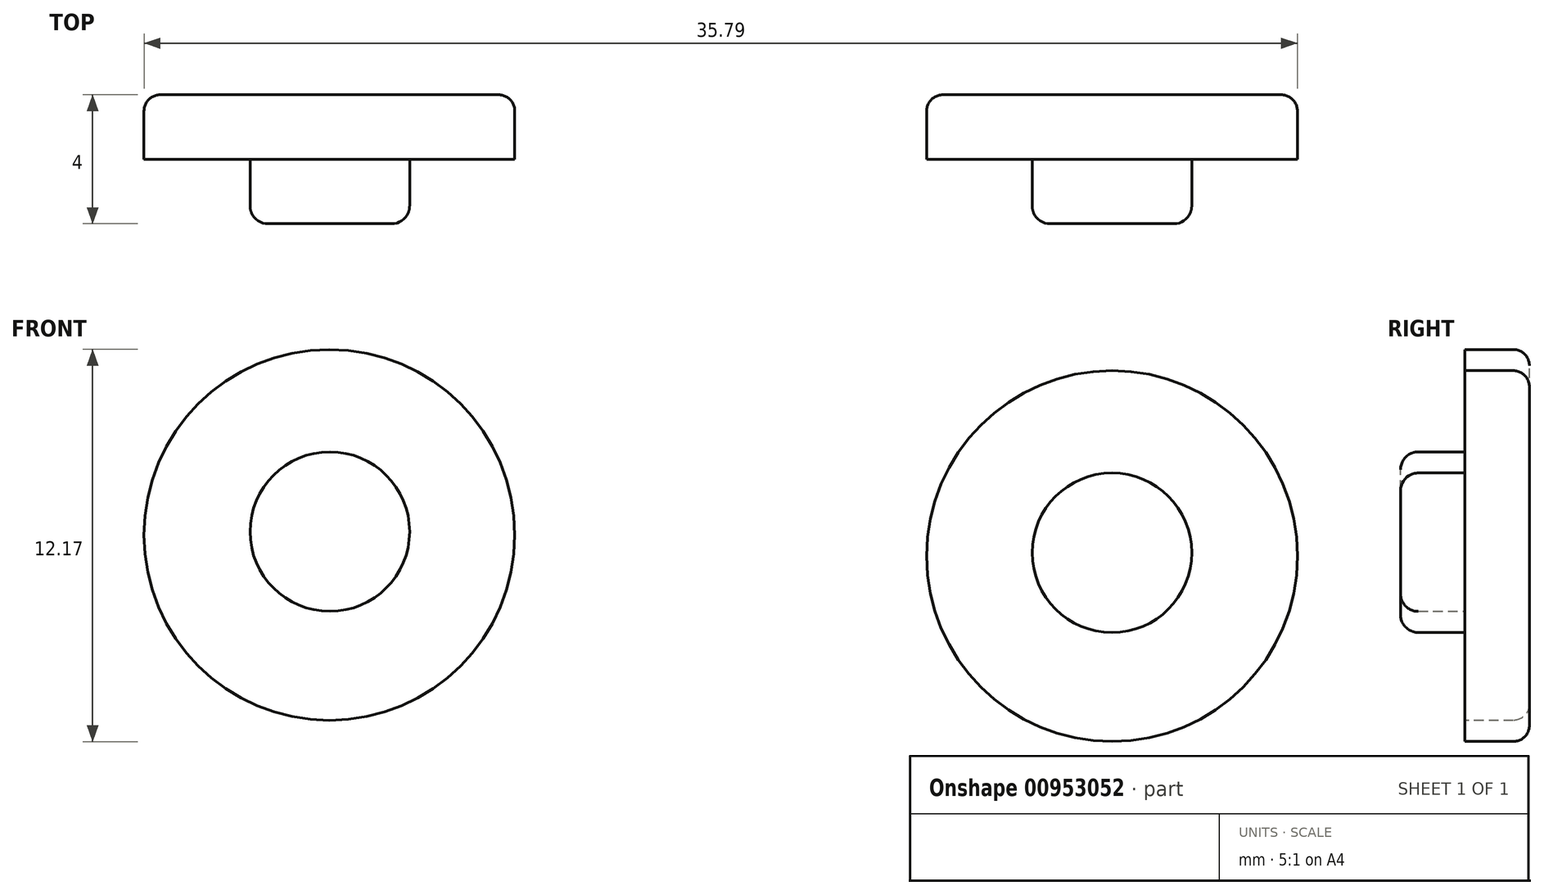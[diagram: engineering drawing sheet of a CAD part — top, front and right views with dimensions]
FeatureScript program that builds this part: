
annotation { "Feature Type Name" : "Feature", "Feature Type Description" : "" }
export const myFeature = defineFeature(function(context is Context, id is Id, definition is map)
    precondition{}
    {
        {
            var Q0;
            Q0=qCreatedBy(makeId("Front.planeOp"),FACE);
            var sketch = newSketch(context, id + "F0", { "sketchPlane" : qUnion([Q0])});
            skCircle(sketch, "E0", {"center": v(-55.31, 54.57) * mm, "radius": 5.75 * mm});
            skCircle(sketch, "E1", {"center": v(-31.02, 53.92) * mm, "radius": 5.75 * mm});
            skSolve(sketch);
        }
        {
            var Q0;
            Q0=makeQuery(id+"F0.imprint","IMPRINT",FACE,{"disambiguationData":[TD([[makeQuery(id+"F0.imprint","IMPRINT",EDGE,{"derivedFrom":sQuery(id+"F0.wireOp",EDGE,"E1")}),1.0]])]});
            var Q1;
            Q1=makeQuery(id+"F0.imprint","IMPRINT",FACE,{"disambiguationData":[TD([[makeQuery(id+"F0.imprint","IMPRINT",EDGE,{"derivedFrom":sQuery(id+"F0.wireOp",EDGE,"E0")}),1.0]])]});
            extrude(context, id + "F1", {"entities" : qUnion([Q0, Q1]), "depth" : -2 * mm, "offsetDistance" : 25.4 * mm});
        }
        {
            var Q0;
            Q0=makeQuery(id+"F1.opExtrude","CAP_EDGE",EDGE,{"disambiguationData":[OSD([sQuery(id+"F0.wireOp",EDGE,"E1")])],"isStart":false});
            var Q1;
            Q1=makeQuery(id+"F1.opExtrude","CAP_EDGE",EDGE,{"disambiguationData":[OSD([sQuery(id+"F0.wireOp",EDGE,"E0")])],"isStart":false});
            fillet(context, id + "F2", {"entities" : qUnion([Q0, Q1]), "radius" : .5 * mm, "tangentPropagation" : true, "allowEdgeOverflow" : false});
        }
        {
            var Q0;
            Q0=qCreatedBy(makeId("Front.planeOp"),FACE);
            var sketch = newSketch(context, id + "F3", { "sketchPlane" : qUnion([Q0])});
            skCircle(sketch, "E2", {"center": v(-55.3, 54.68) * mm, "radius": 2.48 * mm});
            skCircle(sketch, "E3", {"center": v(-31.03, 54.02) * mm, "radius": 2.48 * mm});
            skSolve(sketch);
        }
        {
            var Q0;
            Q0=makeQuery(id+"F3.imprint","IMPRINT",FACE,{"disambiguationData":[TD([[makeQuery(id+"F3.imprint","IMPRINT",EDGE,{"derivedFrom":sQuery(id+"F3.wireOp",EDGE,"E2")}),1.0]])]});
            var Q1;
            Q1=makeQuery(id+"F3.imprint","IMPRINT",FACE,{"disambiguationData":[TD([[makeQuery(id+"F3.imprint","IMPRINT",EDGE,{"derivedFrom":sQuery(id+"F3.wireOp",EDGE,"E3")}),1.0]])]});
            extrude(context, id + "F4", {"entities" : qUnion([Q0, Q1]), "depth" : 2 * mm, "offsetDistance" : 25.4 * mm});
        }
        {
            var Q0;
            Q0=makeQuery(id+"F4.opExtrude","CAP_EDGE",EDGE,{"disambiguationData":[OSD([sQuery(id+"F3.wireOp",EDGE,"E2")])],"isStart":false});
            var Q1;
            Q1=makeQuery(id+"F4.opExtrude","CAP_EDGE",EDGE,{"disambiguationData":[OSD([sQuery(id+"F3.wireOp",EDGE,"E3")])],"isStart":false});
            fillet(context, id + "F5", {"entities" : qUnion([Q0, Q1]), "radius" : .55 * mm, "tangentPropagation" : true, "allowEdgeOverflow" : false});
        }
    });
